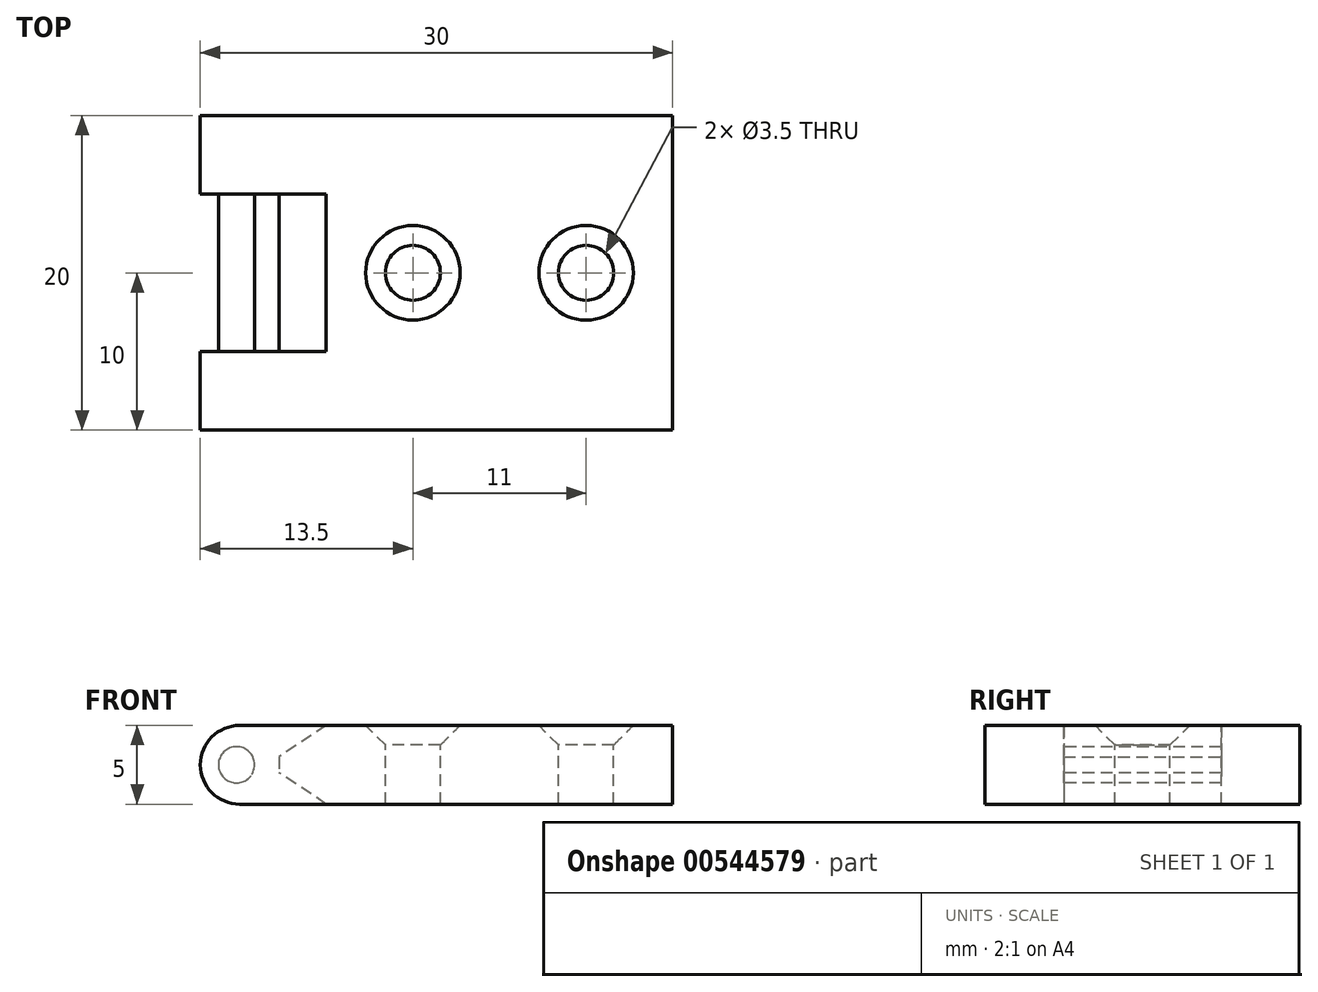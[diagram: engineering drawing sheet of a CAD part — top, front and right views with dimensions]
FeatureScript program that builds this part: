
annotation { "Feature Type Name" : "Feature", "Feature Type Description" : "" }
export const myFeature = defineFeature(function(context is Context, id is Id, definition is map)
    precondition{}
    {
        {
            var Q0;
            Q0=qCreatedBy(makeId("Top.planeOp"),FACE);
            var sketch = newSketch(context, id + "F0", { "sketchPlane" : qUnion([Q0])});
            skLineSegment(sketch, "E0.bottom", {"start": v(12.5, -10) * mm, "end": v(-12.5, -10) * mm});
            skLineSegment(sketch, "E0.top", {"start": v(12.5, 10) * mm, "end": v(-12.5, 10) * mm});
            skLineSegment(sketch, "E0.left", {"start": v(12.5, -10) * mm, "end": v(12.5, 10) * mm});
            skLineSegment(sketch, "E0.right", {"start": v(-12.5, -10) * mm, "end": v(-12.5, 10) * mm});
            skPoint(sketch, "E0.middle", {"position": v(0, 0) * mm});
            skSolve(sketch);
        }
        {
            var Q0;
            Q0=makeQuery(id+"F0.imprint","IMPRINT",FACE,{"disambiguationData":[TD([[makeQuery(id+"F0.imprint","IMPRINT",EDGE,{"derivedFrom":sQuery(id+"F0.wireOp",EDGE,"E0.bottom")}),-1.0]])]});
            extrude(context, id + "F1", {"entities" : qUnion([Q0]), "endBound" : BoundingType.SYMMETRIC, "depth" : 5 * mm, "offsetDistance" : 25 * mm});
        }
        {
            var Q0;
            Q0=makeQuery(id+"F1.opExtrude","SWEPT_FACE",FACE,{"disambiguationData":[OSD([sQuery(id+"F0.wireOp",EDGE,"E0.top")])]});
            var sketch = newSketch(context, id + "F2", { "sketchPlane" : qUnion([Q0])});
            skLineSegment(sketch, "E1", {"start": v(12.5, 0) * mm, "end": v(15, 0) * mm, "construction": true});
            skPoint(sketch, "E1.endSnap0", {"position": v(12.5, 0) * mm});
            skCircle(sketch, "E2", {"center": v(15, 0) * mm, "radius": 2.5 * mm});
            skLineSegment(sketch, "E3", {"start": v(15, 3.09) * mm, "end": v(15, -3.31) * mm, "construction": true});
            skLineSegment(sketch, "E4", {"start": v(12.5, 2.5) * mm, "end": v(15, 2.5) * mm});
            skLineSegment(sketch, "E5", {"start": v(12.5, -2.5) * mm, "end": v(15, -2.5) * mm});
            skLineSegment(sketch, "E6", {"start": v(12.5, 2.5) * mm, "end": v(12.5, -2.5) * mm});
            skSolve(sketch);
        }
        {
            var Q0;
            Q0 = qSketchRegion(id + "F2", true);
            extrude(context, id + "F3", {"entities" : qUnion([Q0]), "operationType" : NewBodyOperationType.ADD, "oppositeDirection" : true, "depth" : 5 * mm, "offsetDistance" : 25 * mm});
        }
        {
            var Q0;
            Q0=makeQuery(id+"F1.opExtrude","SWEPT_FACE",FACE,{"disambiguationData":[OSD([sQuery(id+"F0.wireOp",EDGE,"E0.bottom")])]});
            var sketch = newSketch(context, id + "F4", { "sketchPlane" : qUnion([Q0])});
            skLineSegment(sketch, "E7", {"start": v(-12.5, 0) * mm, "end": v(-15, 0) * mm, "construction": true});
            skPoint(sketch, "E7.endSnap0", {"position": v(-12.5, 0) * mm});
            skCircle(sketch, "E8", {"center": v(-15, 0) * mm, "radius": 2.5 * mm});
            skLineSegment(sketch, "E9", {"start": v(-15, -3.09) * mm, "end": v(-15, 3.31) * mm, "construction": true});
            skLineSegment(sketch, "E10", {"start": v(-12.5, -2.5) * mm, "end": v(-15, -2.5) * mm});
            skLineSegment(sketch, "E11", {"start": v(-12.5, 2.5) * mm, "end": v(-15, 2.5) * mm});
            skLineSegment(sketch, "E12", {"start": v(-12.5, -2.5) * mm, "end": v(-12.5, 2.5) * mm});
            skSolve(sketch);
        }
        {
            var Q0;
            Q0 = qSketchRegion(id + "F4", true);
            extrude(context, id + "F5", {"entities" : qUnion([Q0]), "operationType" : NewBodyOperationType.ADD, "oppositeDirection" : true, "depth" : 5 * mm, "offsetDistance" : 25 * mm});
        }
        {
            var Q0;
            Q0=makeQuery(id+"F5.opExtrude","CAP_FACE",FACE,{"disambiguationData":[OSD([sQuery(id+"F4.wireOp",EDGE,"E8"),sQuery(id+"F4.wireOp",EDGE,"E10"),sQuery(id+"F4.wireOp",EDGE,"E11"),sQuery(id+"F4.wireOp",EDGE,"E12")])],"isStart":false});
            var sketch = newSketch(context, id + "F6", { "sketchPlane" : qUnion([Q0])});
            skLineSegment(sketch, "E13", {"start": v(15.2, 2.5) * mm, "end": v(15.2, -2.5) * mm, "construction": true});
            skPoint(sketch, "E14", {"position": v(15.2, 0) * mm});
            skCircle(sketch, "E15", {"center": v(15.2, 0) * mm, "radius": 1.15 * mm});
            skSolve(sketch);
        }
        {
            var Q0;
            Q0 = qSketchRegion(id + "F6", true);
            extrude(context, id + "F7", {"entities" : qUnion([Q0]), "operationType" : NewBodyOperationType.ADD, "depth" : 10 * mm, "offsetDistance" : 25 * mm});
        }
        {
            var Q0;
            Q0=makeQuery(id+"F1.opExtrude","CAP_EDGE",EDGE,{"disambiguationData":[OSD([sQuery(id+"F0.wireOp",EDGE,"E0.right")])],"isStart":true});
            var Q1;
            Q1=makeQuery(id+"F1.opExtrude","CAP_EDGE",EDGE,{"disambiguationData":[OSD([sQuery(id+"F0.wireOp",EDGE,"E0.right")])],"isStart":false});
            chamfer(context, id + "F8", {"entities" : qUnion([Q0, Q1]), "chamferType" : ChamferType.TWO_OFFSETS, "width1" : 3 * mm, "oppositeDirection" : false, "width2" : 2 * mm, "tangentPropagation" : true});
        }
        {
            var Q0;
            Q0=makeQuery(id+"F5.boolean.opBoolean","MERGE",FACE,{"derivedFrom":[makeQuery(id+"F3.boolean.opBoolean","MERGE",FACE,{"derivedFrom":[makeQuery(id+"F1.opExtrude","CAP_FACE",FACE,{"disambiguationData":[OSD([sQuery(id+"F0.wireOp",EDGE,"E0.bottom"),sQuery(id+"F0.wireOp",EDGE,"E0.top"),sQuery(id+"F0.wireOp",EDGE,"E0.left"),sQuery(id+"F0.wireOp",EDGE,"E0.right")])],"isStart":false}),makeQuery(id+"F3.opExtrude","SWEPT_FACE",FACE,{"disambiguationData":[OSD([sQuery(id+"F2.wireOp",EDGE,"E4")])]})]}),makeQuery(id+"F5.opExtrude","SWEPT_FACE",FACE,{"disambiguationData":[OSD([sQuery(id+"F4.wireOp",EDGE,"E11")])]})]});
            var sketch = newSketch(context, id + "F9", { "sketchPlane" : qUnion([Q0])});
            skLineSegment(sketch, "E16", {"start": v(-17.97, 0) * mm, "end": v(16.12, 0) * mm, "construction": true});
            skPoint(sketch, "E16.startSnap0", {"position": v(-9.5, 0) * mm});
            skCircle(sketch, "E17", {"center": v(1.5, 0) * mm, "radius": 5.5 * mm, "construction": true});
            skPoint(sketch, "E18", {"position": v(12.5, 0) * mm});
            skPoint(sketch, "E19", {"position": v(-4, 0) * mm});
            skPoint(sketch, "E20", {"position": v(7, 0) * mm});
            skSolve(sketch);
        }
        {
            var Q0;
            Q0=sQuery(id+"F9.wireOp",VERTEX,"E19");
            var Q1;
            Q1=sQuery(id+"F9.wireOp",VERTEX,"E20");
            var Q2;
            Q2=makeQuery(id+"F1.opExtrude","SWEPT_BODY",BODY,{"disambiguationData":[OSD([sQuery(id+"F0.wireOp",EDGE,"E0.bottom"),sQuery(id+"F0.wireOp",EDGE,"E0.top"),sQuery(id+"F0.wireOp",EDGE,"E0.left"),sQuery(id+"F0.wireOp",EDGE,"E0.right")])]});
            hole(context, id + "F10", {"style" : HoleStyle.C_SINK, "endStyle" : HoleEndStyle.THROUGH, "holeDiameter" : 3.5 * mm, "cSinkDiameter" : 6 * mm, "cSinkAngle" : 90 * degree, "isTappedThrough" : true, "tappedDepth" : 12 * mm, "tapClearance" : 3, "locations" : qUnion([Q0, Q1]), "scope" : qUnion([Q2])});
        }
    });
